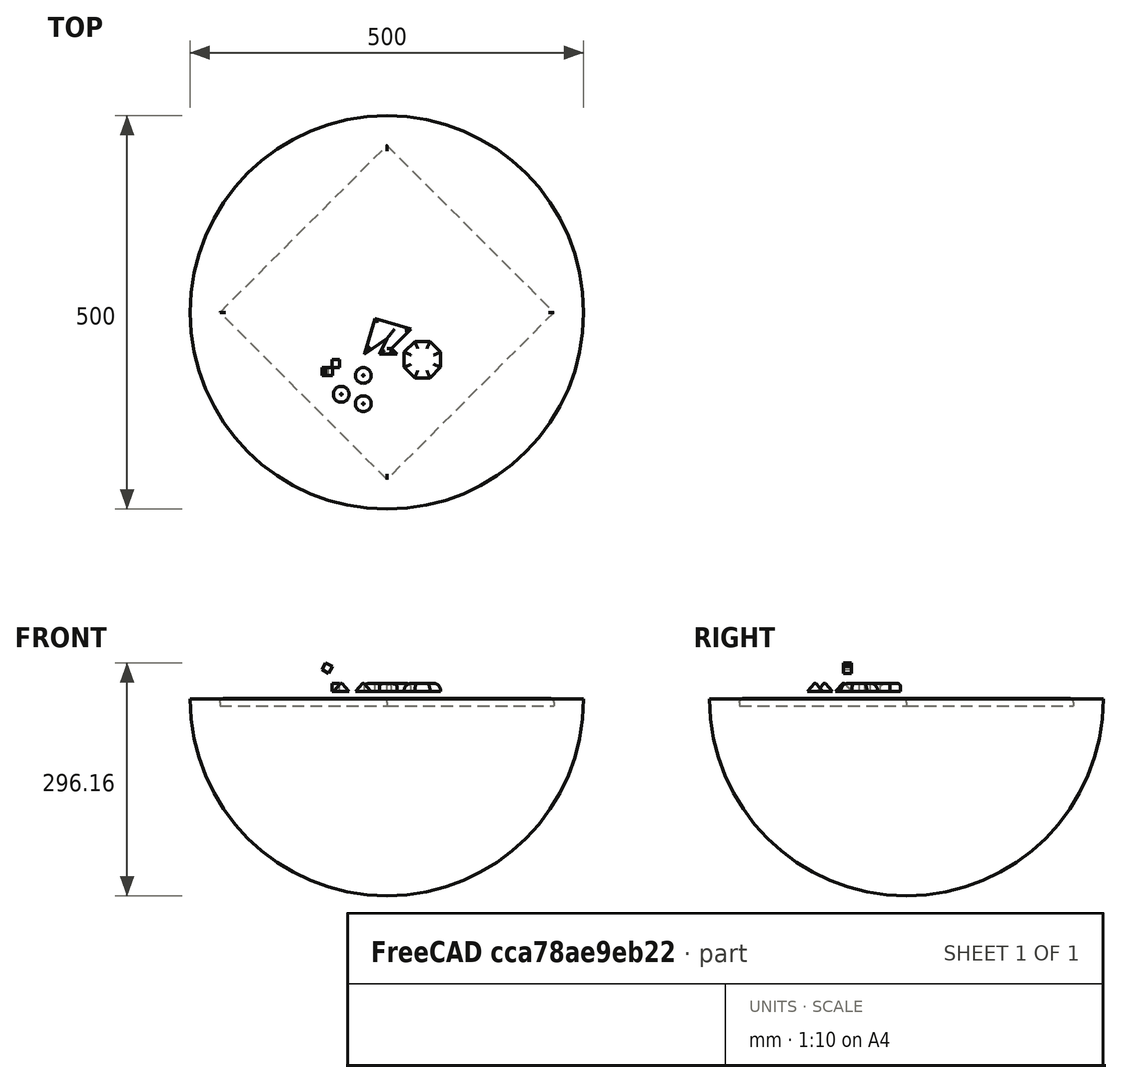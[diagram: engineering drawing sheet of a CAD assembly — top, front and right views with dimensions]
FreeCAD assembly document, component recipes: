
FREECAD ASSEMBLY — COMPONENT RECIPES ("assembly")

This assembly document has 7 components, labeled P0..P6 below (a component is one placed body or linked part). 5 of them carry a construction recipe — the FreeCAD feature program that regenerates the part from scratch, quoted from this document or its linked companion documents; the rest are supplied as boundary geometry only. No exploded tour is included for this assembly.
COMPONENT P0 — recipe-attached ("root_body", modeled in this document).
Construction recipe (the document's own serialized feature program — sketch geometry with constraints, then the solid features built on it; lengths are millimeters unless a unit is written):

FEATURE [Sketcher::SketchObject] Sketch002
  MapMode = 5
  Support = -> [XY_Plane005]
  sketch-geometry (7):
    g0: LineSegment StartX=-15.1232 StartY=25.4281 StartZ=0 EndX=-28.6703 EndY=-20.0752 EndZ=0
    g1: LineSegment StartX=-28.6703 StartY=-20.0752 StartZ=0 EndX=-3.6e-15 EndY=0 EndZ=0
    g2: LineSegment StartX=-3.6e-15 StartY=0 StartZ=0 EndX=-9.2976 EndY=-19.9388 EndZ=0
    g3: LineSegment StartX=-9.2976 StartY=-19.9388 StartZ=0 EndX=12.7024 EndY=-19.9388 EndZ=0
    g4: LineSegment StartX=12.7024 StartY=-19.9388 StartZ=0 EndX=5.63133 EndY=-12.8677 EndZ=0
    g5: LineSegment StartX=5.63133 StartY=-12.8677 StartZ=0 EndX=30.3801 EndY=11.881 EndZ=0
    g6: LineSegment StartX=30.3801 StartY=11.881 StartZ=0 EndX=-15.1232 EndY=25.4281 EndZ=0
  constraints (20):
    c: Coincident(g0,g1)
    c: Coincident(g1,g2)
    c: Coincident(g2,g3)
    c: Coincident(g3,g4)
    c: Coincident(g4,g5)
    c: Coincident(g5,g6)
    c: Coincident(g6,g0)
    c: Coincident(g1,g-1)
    c: Perpendicular(g5,g4)
    c: Perpendicular(g6,g0)
    c: Equal(g0,g6)
    c: Equal(g2,g3)
    c: Equal(g1,g5)
    c: Angle(g1,g2) = 0.523599
    c: Angle(g4,g3) = 0.785398
    c: Horizontal(g3)
    c: Distance(g4) = 10
    c: Distance(g1) = 35
    c: Angle(g3,g2) = 1.13446
    c: Distance(g2) = 22
FEATURE [PartDesign::Pad] Pad002
  Length = 10
  Length2 = 100
  Profile = -> Sketch002
  Type = 0
FEATURE [PartDesign::Fillet] Fillet002
  Base = -> Pad002 [Face9]
  BaseFeature = -> Pad002
  Radius = 4
FEATURE [PartDesign::Body] Body002  label="root_body"
  Group = -> [Sketch002,Pad002,Fillet002]
  Origin = -> Origin005
  Placement = pos=(0,-33,0) rot=(0,0,1;0rad)
  Tip = -> Fillet002
COMPONENT P1 — recipe-attached ("cube_part_clone_Body", modeled in this document).
Construction recipe (the document's own serialized feature program — sketch geometry with constraints, then the solid features built on it; lengths are millimeters unless a unit is written):

FEATURE [PartDesign::FeatureBase] Clone  label="cube_part_clone"
  BaseFeature = -> Box001
  Placement = pos=(-55,-57,0) rot=(0,0,1;0rad)
FEATURE [PartDesign::Body] Body003  label="cube_part_clone_Body"
  BaseFeature = -> Box001
  Group = -> [Clone]
  Origin = -> Origin006
  Placement = pos=(-35,-23,0) rot=(0,1,0;0.523599rad)
  Tip = -> Clone
COMPONENT P2 — recipe-attached ("floor_body_clone_Body", modeled in this document).
Construction recipe (the document's own serialized feature program — sketch geometry with constraints, then the solid features built on it; lengths are millimeters unless a unit is written):

FEATURE [PartDesign::FeatureBase] Clone001  label="floor_body_clone"
  BaseFeature = -> Body
FEATURE [PartDesign::Body] Body004  label="floor_body_clone_Body"
  BaseFeature = -> Body
  Group = -> [Clone001]
  Origin = -> Origin007
  Placement = pos=(0,0,-9) rot=(0,0,1;0.785398rad)
  Tip = -> Clone001
COMPONENT P3 — geometry summary ("my_final_assembly"; no construction recipe available for this part):
  bounding box: 160.0 x 150.0 x 21.0 mm
  tessellated surface: 131,360 triangles
  volume: 247423 mm^3 (49% of its bounding box)
COMPONENT P4 — recipe-attached ("octagon_part", modeled in this document).
Construction recipe (the document's own serialized feature program — sketch geometry with constraints, then the solid features built on it; lengths are millimeters unless a unit is written):

FEATURE [Sketcher::SketchObject] Sketch001  label="octagon_sketch"
  MapMode = 5
  Support = -> [XY_Plane003]
  sketch-geometry (9):
    g0: LineSegment StartX=23.097 StartY=-9.56709 StartZ=0 EndX=23.097 EndY=9.56709 EndZ=0
    g1: LineSegment StartX=23.097 StartY=9.56709 StartZ=0 EndX=9.56709 EndY=23.097 EndZ=0
    g2: LineSegment StartX=9.56709 StartY=23.097 StartZ=0 EndX=-9.56709 EndY=23.097 EndZ=0
    g3: LineSegment StartX=-9.56709 StartY=23.097 StartZ=0 EndX=-23.097 EndY=9.56709 EndZ=0
    g4: LineSegment StartX=-23.097 StartY=9.56709 StartZ=0 EndX=-23.097 EndY=-9.56709 EndZ=0
    g5: LineSegment StartX=-23.097 StartY=-9.56709 StartZ=0 EndX=-9.56709 EndY=-23.097 EndZ=0
    g6: LineSegment StartX=-9.56709 StartY=-23.097 StartZ=0 EndX=9.56709 EndY=-23.097 EndZ=0
    g7: LineSegment StartX=9.56709 StartY=-23.097 StartZ=0 EndX=23.097 EndY=-9.56709 EndZ=0
    g8: Circle [constr] CenterX=0 CenterY=0 CenterZ=0 NormalX=0 NormalY=0 NormalZ=1 AngleXU=0 Radius=25
  constraints (20):
    c: Coincident(g0,g1)
    c: Coincident(g1,g2)
    c: Coincident(g2,g3)
    c: Coincident(g3,g4)
    c: Coincident(g4,g5)
    c: Coincident(g5,g6)
    c: Coincident(g6,g7)
    c: Coincident(g7,g0)
    c: Equal(g0, g1-g7) x7
    c: PointOnObject(g0,g8)
    c: PointOnObject(g1,g8)
    c: PointOnObject(g2,g8)
    c: PointOnObject(g3,g8)
    c: PointOnObject(g4,g8)
    c: PointOnObject(g5,g8)
    c: PointOnObject(g6,g8)
    c: PointOnObject(g7,g8)
    c: Coincident(g8,g-1)
    c: Horizontal(g6)
    c: Radius(g8) = 25
FEATURE [PartDesign::Pad] Pad001  label="octagon_Pad"
  Length = 10
  Length2 = 100
  Profile = -> Sketch001
  Type = 0
FEATURE [PartDesign::Fillet] Fillet  label="octagon_Fillet"
  Base = -> Pad001 [Face10]
  BaseFeature = -> Pad001
  Radius = 9
FEATURE [PartDesign::Body] Body001  label="octagon_body"
  Group = -> [Sketch001,Pad001,Fillet]
  Origin = -> Origin003
  Placement = pos=(45,-60,0) rot=(0,0,1;0rad)
  Tip = -> Fillet
COMPONENT P5 — recipe-attached ("floor_part", modeled in this document).
Construction recipe (the document's own serialized feature program — sketch geometry with constraints, then the solid features built on it; lengths are millimeters unless a unit is written):

FEATURE [Sketcher::SketchObject] Sketch  label="floor_Sketch"
  MapMode = 5
  Support = -> [XY_Plane001]
  sketch-geometry (4):
    g0: LineSegment StartX=-150 StartY=150 StartZ=0 EndX=150 EndY=150 EndZ=0
    g1: LineSegment StartX=150 StartY=150 StartZ=0 EndX=150 EndY=-150 EndZ=0
    g2: LineSegment StartX=150 StartY=-150 StartZ=0 EndX=-150 EndY=-150 EndZ=0
    g3: LineSegment StartX=-150 StartY=-150 StartZ=0 EndX=-150 EndY=150 EndZ=0
  constraints (11):
    c: Coincident(g0,g1)
    c: Coincident(g1,g2)
    c: Coincident(g2,g3)
    c: Coincident(g3,g0)
    c: Horizontal(g0)
    c: Horizontal(g2)
    c: Vertical(g1)
    c: Vertical(g3)
    c: Symmetric(g0,g1,g-1)
    c: Equal(g0,g3)
    c: DistanceX(g2,g2) = 300
FEATURE [PartDesign::Pad] Pad  label="floor_Pad"
  Length = 10
  Length2 = 100
  Profile = -> Sketch
  Reversed = true
  Type = 0
FEATURE [PartDesign::Fillet] Fillet001
  Base = -> Pad [Face5]
  BaseFeature = -> Pad
  Radius = 5
FEATURE [PartDesign::Body] Body  label="floor_body"
  Group = -> [Sketch,Pad,Fillet001]
  Origin = -> Origin001
  Tip = -> Fillet001
COMPONENT P6 — geometry summary ("deco_Part"; no construction recipe available for this part):
  bounding box: 79.0 x 48.0 x 10.0 mm
  tessellated surface: 3,210 triangles
  volume: 4487 mm^3 (12% of its bounding box)
PROVENANCE & LICENSES
A FreeCAD (.FCStd) document from a public repository crawl; recipes are the document's own serialized feature recipes (and, for linked parts, companion documents' recipes).
License: mit.
